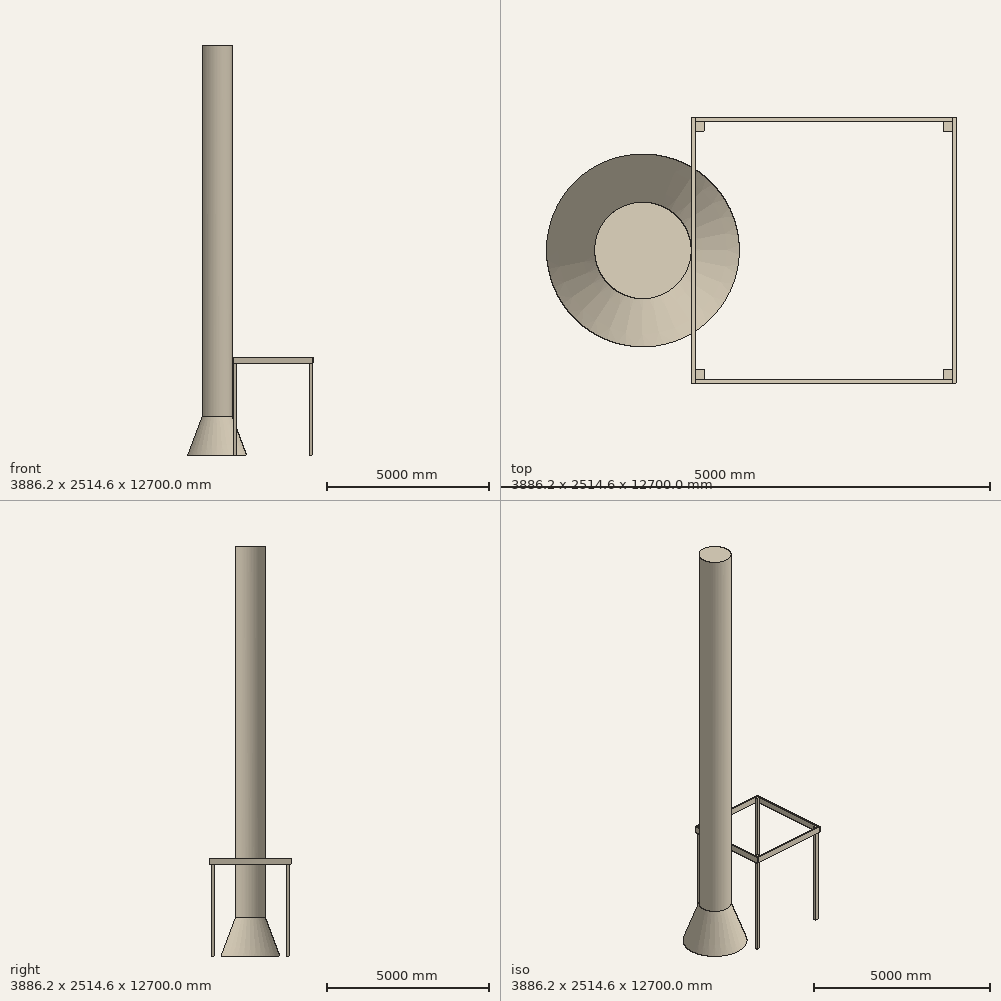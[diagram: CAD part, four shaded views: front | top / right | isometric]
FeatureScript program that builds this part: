
annotation { "Feature Type Name" : "Feature", "Feature Type Description" : "" }
export const myFeature = defineFeature(function(context is Context, id is Id, definition is map)
    precondition{}
    {
        {
            var Q0;
            Q0=qCreatedBy(makeId("Top.planeOp"),FACE);
            var sketch = newSketch(context, id + "F0", { "sketchPlane" : qUnion([Q0])});
            skCircle(sketch, "E0", {"center": v(0, 0) * mm, "radius": 457.2 * mm});
            skSolve(sketch);
        }
        {
            var Q0;
            Q0 = qSketchRegion(id + "F0", true);
            extrude(context, id + "F1", {"entities" : qUnion([Q0]), "depth" : 12700 * mm, "offsetDistance" : 25.4 * mm});
        }
        {
            var Q0;
            Q0=qCreatedBy(makeId("Right.planeOp"),FACE);
            var sketch = newSketch(context, id + "F2", { "sketchPlane" : qUnion([Q0])});
            skLineSegment(sketch, "E1", {"start": v(0, 0) * mm, "end": v(0, 1531.39) * mm, "construction": true});
            skLineSegment(sketch, "E2", {"start": v(0, 2438.4) * mm, "end": v(-914.4, 0) * mm});
            skLineSegment(sketch, "E3", {"start": v(-914.4, 0) * mm, "end": v(0, 0) * mm});
            skLineSegment(sketch, "E4", {"start": v(0, 0) * mm, "end": v(0, 2438.4) * mm});
            skSolve(sketch);
        }
        {
            var Q0;
            Q0 = qSketchRegion(id + "F2", true);
            var Q1;
            Q1=sQuery(id+"F2.wireOp",EDGE,"E1");
            revolve(context, id + "F3", {"operationType" : NewBodyOperationType.ADD, "surfaceOperationType" : NewSurfaceOperationType.NEW, "entities" : qUnion([Q0]), "axis" : qUnion([Q1]), "revolveType" : RevolveType.FULL});
        }
        {
            var Q0;
            Q0=qCreatedBy(makeId("Top.planeOp"),FACE);
            var sketch = newSketch(context, id + "F4", { "sketchPlane" : qUnion([Q0])});
            skLineSegment(sketch, "E5", {"start": v(0, 0) * mm, "end": v(2933.7, 0) * mm, "construction": true});
            skLineSegment(sketch, "E6", {"start": v(1714.5, -2963.68) * mm, "end": v(1714.5, 0) * mm, "construction": true});
            skLineSegment(sketch, "E7.bottom", {"start": v(2933.7, -1219.2) * mm, "end": v(2844.8, -1219.2) * mm});
            skLineSegment(sketch, "E7.top", {"start": v(2933.7, -1130.3) * mm, "end": v(2844.8, -1130.3) * mm});
            skLineSegment(sketch, "E7.left", {"start": v(2933.7, -1219.2) * mm, "end": v(2933.7, -1130.3) * mm});
            skLineSegment(sketch, "E7.right", {"start": v(2844.8, -1219.2) * mm, "end": v(2844.8, -1130.3) * mm});
            skLineSegment(sketch, "E8.MirrorCS", {"start": v(584.2, -1219.2) * mm, "end": v(584.2, -1130.3) * mm});
            skLineSegment(sketch, "E9.MirrorCS", {"start": v(495.3, -1130.3) * mm, "end": v(584.2, -1130.3) * mm});
            skLineSegment(sketch, "E10.MirrorCS", {"start": v(495.3, -1219.2) * mm, "end": v(495.3, -1130.3) * mm});
            skLineSegment(sketch, "E11.MirrorCS", {"start": v(495.3, -1219.2) * mm, "end": v(584.2, -1219.2) * mm});
            skSolve(sketch);
        }
        {
            var Q0;
            Q0 = qSketchRegion(id + "F4", true);
            extrude(context, id + "F5", {"entities" : qUnion([Q0]), "depth" : 3048 * mm, "offsetDistance" : 25.4 * mm});
        }
        {
            var Q0;
            Q0=makeQuery(id+"F5.opExtrude","SWEPT_BODY",BODY,{"disambiguationData":[OSD([sQuery(id+"F4.wireOp",EDGE,"E7.bottom"),sQuery(id+"F4.wireOp",EDGE,"E7.top"),sQuery(id+"F4.wireOp",EDGE,"E7.left"),sQuery(id+"F4.wireOp",EDGE,"E7.right")])]});
            var Q1;
            Q1=makeQuery(id+"F5.opExtrude","SWEPT_BODY",BODY,{"disambiguationData":[OSD([sQuery(id+"F4.wireOp",EDGE,"E8.MirrorCS"),sQuery(id+"F4.wireOp",EDGE,"E9.MirrorCS"),sQuery(id+"F4.wireOp",EDGE,"E10.MirrorCS"),sQuery(id+"F4.wireOp",EDGE,"E11.MirrorCS")])]});
            var Q2;
            Q2=qCreatedBy(makeId("Front.planeOp"),FACE);
            mirror(context, id + "F6", {"entities" : qUnion([Q0, Q1]), "mirrorPlane" : qUnion([Q2])});
        }
        {
            var Q0;
            Q0=makeQuery(id+"F6.opPattern","COPY",FACE,{"derivedFrom":makeQuery(id+"F5.opExtrude","SWEPT_FACE",FACE,{"disambiguationData":[OSD([sQuery(id+"F4.wireOp",EDGE,"E7.left")])]}),"instanceName":"1"});
            var sketch = newSketch(context, id + "F7", { "sketchPlane" : qUnion([Q0])});
            skLineSegment(sketch, "E12.bottom", {"start": v(1257.3, 3048) * mm, "end": v(-1257.3, 3048) * mm});
            skLineSegment(sketch, "E12.top", {"start": v(1257.3, 2857.5) * mm, "end": v(-1257.3, 2857.5) * mm});
            skLineSegment(sketch, "E12.left", {"start": v(1257.3, 3048) * mm, "end": v(1257.3, 2857.5) * mm});
            skLineSegment(sketch, "E12.right", {"start": v(-1257.3, 3048) * mm, "end": v(-1257.3, 2857.5) * mm});
            skSolve(sketch);
        }
        {
            var Q0;
            Q0 = qSketchRegion(id + "F7", true);
            extrude(context, id + "F8", {"entities" : qUnion([Q0]), "depth" : 38.1 * mm, "offsetDistance" : 25.4 * mm});
        }
        {
            var Q0;
            Q0=qCreatedBy(makeId("Right.planeOp"),FACE);
            cPlane(context, id + "F9", {"entities" : qUnion([Q0]), "cplaneType" : CPlaneType.OFFSET, "offset" : 1714.5 * mm, "width" : 152.4 * mm, "height" : 152.4 * mm});
        }
        {
            var Q0;
            Q0=makeQuery(id+"F8.opExtrude","SWEPT_BODY",BODY,{"disambiguationData":[OSD([sQuery(id+"F7.wireOp",EDGE,"E12.bottom"),sQuery(id+"F7.wireOp",EDGE,"E12.top"),sQuery(id+"F7.wireOp",EDGE,"E12.left"),sQuery(id+"F7.wireOp",EDGE,"E12.right")])]});
            var Q1;
            Q1=qCreatedBy(id+"F9.planeOp",FACE);
            mirror(context, id + "F10", {"entities" : qUnion([Q0]), "mirrorPlane" : qUnion([Q1])});
        }
        {
            var Q0;
            Q0=makeQuery(id+"F5.opExtrude","SWEPT_FACE",FACE,{"disambiguationData":[OSD([sQuery(id+"F4.wireOp",EDGE,"E7.bottom")])]});
            var sketch = newSketch(context, id + "F11", { "sketchPlane" : qUnion([Q0])});
            skLineSegment(sketch, "E13.bottom", {"start": v(2933.7, 3048) * mm, "end": v(495.3, 3048) * mm});
            skLineSegment(sketch, "E13.top", {"start": v(2933.7, 2857.5) * mm, "end": v(495.3, 2857.5) * mm});
            skLineSegment(sketch, "E13.left", {"start": v(2933.7, 3048) * mm, "end": v(2933.7, 2857.5) * mm});
            skLineSegment(sketch, "E13.right", {"start": v(495.3, 3048) * mm, "end": v(495.3, 2857.5) * mm});
            skSolve(sketch);
        }
        {
            var Q0;
            Q0 = qSketchRegion(id + "F11", true);
            extrude(context, id + "F12", {"entities" : qUnion([Q0]), "depth" : 38.1 * mm, "offsetDistance" : 25.4 * mm});
        }
        {
            var Q0;
            Q0=makeQuery(id+"F12.opExtrude","SWEPT_BODY",BODY,{"disambiguationData":[OSD([sQuery(id+"F11.wireOp",EDGE,"E13.bottom"),sQuery(id+"F11.wireOp",EDGE,"E13.top"),sQuery(id+"F11.wireOp",EDGE,"E13.left"),sQuery(id+"F11.wireOp",EDGE,"E13.right")])]});
            var Q1;
            Q1=qCreatedBy(makeId("Front.planeOp"),FACE);
            mirror(context, id + "F13", {"entities" : qUnion([Q0]), "mirrorPlane" : qUnion([Q1])});
        }
    });
